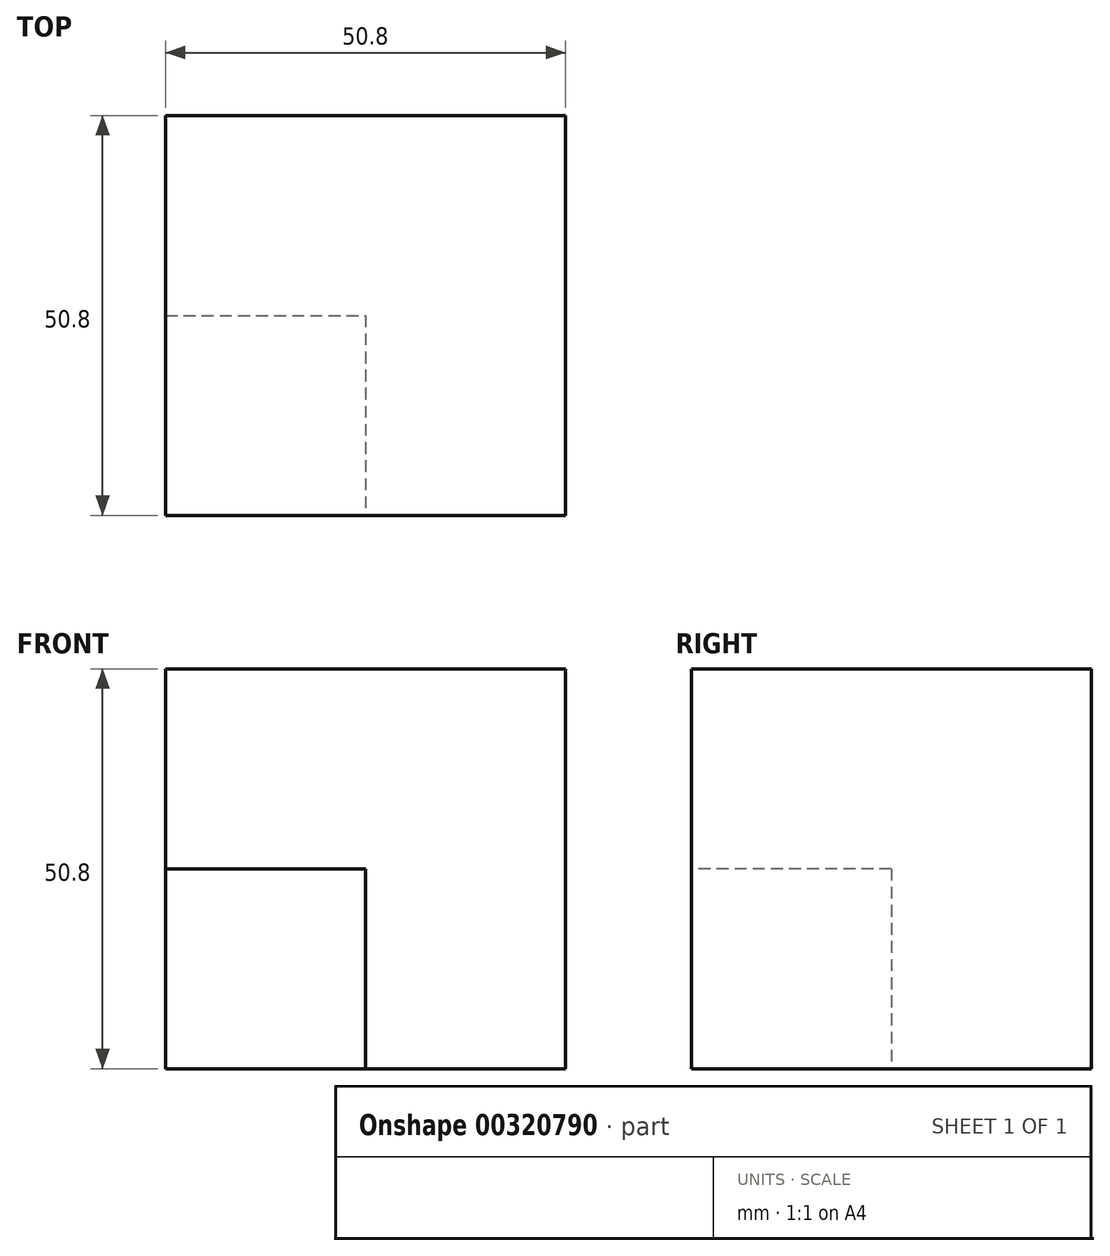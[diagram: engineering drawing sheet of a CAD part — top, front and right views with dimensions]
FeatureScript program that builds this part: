
annotation { "Feature Type Name" : "Feature", "Feature Type Description" : "" }
export const myFeature = defineFeature(function(context is Context, id is Id, definition is map)
    precondition{}
    {
        {
            var Q0;
            Q0=qCreatedBy(makeId("Front.planeOp"),FACE);
            var sketch = newSketch(context, id + "F0", { "sketchPlane" : qUnion([Q0])});
            skLineSegment(sketch, "E0", {"start": v(-64.51, -1.24) * mm, "end": v(-64.51, -52.04) * mm});
            skLineSegment(sketch, "E1", {"start": v(-64.51, -52.04) * mm, "end": v(-13.71, -52.04) * mm});
            skLineSegment(sketch, "E2", {"start": v(-13.71, -52.04) * mm, "end": v(-13.71, -1.24) * mm});
            skLineSegment(sketch, "E3", {"start": v(-13.71, -1.24) * mm, "end": v(-64.51, -1.24) * mm});
            skSolve(sketch);
        }
        {
            var Q0;
            Q0 = qSketchRegion(id + "F0", true);
            var Q1;
            Q1=makeQuery(id+"F0.imprint","IMPRINT",FACE,{"disambiguationData":[TD([[makeQuery(id+"F0.imprint","IMPRINT",EDGE,{"derivedFrom":sQuery(id+"F0.wireOp",EDGE,"E0")}),1.0]])]});
            extrude(context, id + "F1", {"entities" : qUnion([Q0, Q1]), "depth" : 50.8 * mm});
        }
        {
            var Q0;
            Q0=makeQuery(id+"F1.opExtrude","CAP_FACE",FACE,{"disambiguationData":[OSD([sQuery(id+"F0.wireOp",EDGE,"E0"),sQuery(id+"F0.wireOp",EDGE,"E1"),sQuery(id+"F0.wireOp",EDGE,"E2"),sQuery(id+"F0.wireOp",EDGE,"E3")])],"isStart":false});
            var sketch = newSketch(context, id + "F2", { "sketchPlane" : qUnion([Q0])});
            skLineSegment(sketch, "E4", {"start": v(-64.51, -26.64) * mm, "end": v(-39.11, -26.64) * mm});
            skLineSegment(sketch, "E5", {"start": v(-39.11, -26.64) * mm, "end": v(-39.11, -52.04) * mm});
            skLineSegment(sketch, "E6", {"start": v(-64.51, -52.04) * mm, "end": v(-39.11, -52.04) * mm});
            skLineSegment(sketch, "E7", {"start": v(-39.11, -52.04) * mm, "end": v(-64.51, -52.04) * mm});
            skLineSegment(sketch, "E8", {"start": v(-64.51, -26.64) * mm, "end": v(-64.51, -52.04) * mm});
            skSolve(sketch);
        }
        {
            var Q0;
            Q0 = qSketchRegion(id + "F2", true);
            extrude(context, id + "F3", {"entities" : qUnion([Q0]), "operationType" : NewBodyOperationType.REMOVE, "oppositeDirection" : true, "depth" : 25.4 * mm});
        }
    });
